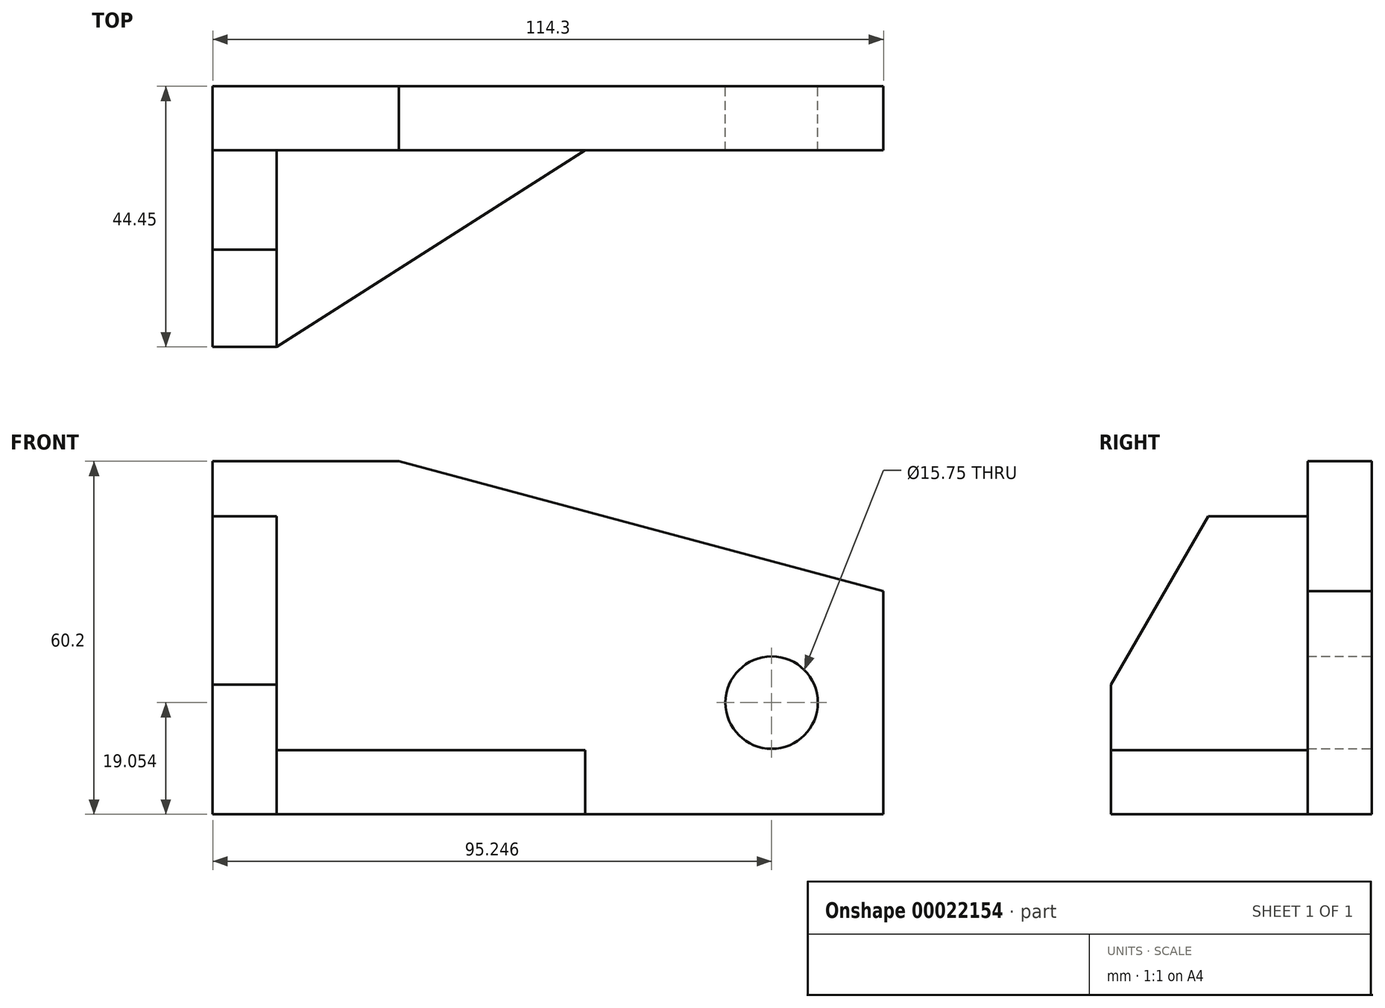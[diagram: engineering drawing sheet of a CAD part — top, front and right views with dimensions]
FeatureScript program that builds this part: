
annotation { "Feature Type Name" : "Feature", "Feature Type Description" : "" }
export const myFeature = defineFeature(function(context is Context, id is Id, definition is map)
    precondition{}
    {
        {
            var Q0;
            Q0=qCreatedBy(makeId("Front.planeOp"),FACE);
            var sketch = newSketch(context, id + "F0", { "sketchPlane" : qUnion([Q0])});
            skLineSegment(sketch, "E0.bottom", {"start": v(-55.11, 32.77) * mm, "end": v(59.19, 32.77) * mm});
            skLineSegment(sketch, "E0.top", {"start": v(-55.11, -27.43) * mm, "end": v(59.19, -27.43) * mm});
            skLineSegment(sketch, "E0.left", {"start": v(-55.11, 32.77) * mm, "end": v(-55.11, -27.43) * mm});
            skLineSegment(sketch, "E0.right", {"start": v(59.19, 32.77) * mm, "end": v(59.19, -27.43) * mm});
            skLineSegment(sketch, "E1", {"start": v(-23.36, 32.77) * mm, "end": v(59.19, 10.65) * mm});
            skCircle(sketch, "E2", {"center": v(40.14, -8.38) * mm, "radius": 7.87 * mm});
            skSolve(sketch);
        }
        {
            var Q0;
            {var subQ2=sQuery(id+"F0.wireOp",EDGE,"E0.top");Q0=makeQuery(id+"F0.imprint","IMPRINT",FACE,{"disambiguationData":[TD([[makeQuery(id+"F0.imprint","IMPRINT",EDGE,{"derivedFrom":subQ2}),1.0]])]});}
            extrude(context, id + "F1", {"entities" : qUnion([Q0]), "depth" : 10.92 * mm});
        }
        {
            var Q0;
            Q0=makeQuery(id+"F1.opExtrude","SWEPT_FACE",FACE,{"disambiguationData":[OSD([sQuery(id+"F0.wireOp",EDGE,"E0.left")])]});
            var sketch = newSketch(context, id + "F2", { "sketchPlane" : qUnion([Q0])});
            skLineSegment(sketch, "E3.bottom", {"start": v(10.92, -27.43) * mm, "end": v(44.45, -27.43) * mm});
            skLineSegment(sketch, "E3.top", {"start": v(10.92, 23.37) * mm, "end": v(44.45, 23.37) * mm});
            skLineSegment(sketch, "E3.left", {"start": v(10.92, -27.43) * mm, "end": v(10.92, 23.37) * mm});
            skLineSegment(sketch, "E3.right", {"start": v(44.45, -27.43) * mm, "end": v(44.45, 23.37) * mm});
            skLineSegment(sketch, "E4", {"start": v(44.45, -5.33) * mm, "end": v(27.88, 23.37) * mm});
            skSolve(sketch);
        }
        {
            var Q0;
            {var subQ2=sQuery(id+"F2.wireOp",EDGE,"E3.bottom");Q0=makeQuery(id+"F2.imprint","IMPRINT",FACE,{"disambiguationData":[TD([[makeQuery(id+"F2.imprint","IMPRINT",EDGE,{"derivedFrom":subQ2}),1.0]])]});}
            extrude(context, id + "F3", {"entities" : qUnion([Q0]), "oppositeDirection" : true, "depth" : 10.92 * mm});
        }
        {
            var Q0;
            Q0=makeQuery(id+"F1.opExtrude","SWEPT_FACE",FACE,{"disambiguationData":[OSD([sQuery(id+"F0.wireOp",EDGE,"E0.top")])]});
            var sketch = newSketch(context, id + "F4", { "sketchPlane" : qUnion([Q0])});
            skLineSegment(sketch, "E5.bottom", {"start": v(-44.2, 44.45) * mm, "end": v(8.39, 44.45) * mm});
            skLineSegment(sketch, "E5.top", {"start": v(-44.2, 10.92) * mm, "end": v(8.39, 10.92) * mm});
            skLineSegment(sketch, "E5.left", {"start": v(-44.2, 44.45) * mm, "end": v(-44.2, 10.92) * mm});
            skLineSegment(sketch, "E5.right", {"start": v(8.39, 44.45) * mm, "end": v(8.39, 10.92) * mm});
            skLineSegment(sketch, "E6", {"start": v(-44.2, 44.45) * mm, "end": v(8.39, 10.92) * mm});
            skSolve(sketch);
        }
        {
            var Q0;
            Q0=makeQuery(id+"F4.imprint","IMPRINT",FACE,{"disambiguationData":[TD([[makeQuery(id+"F4.imprint","IMPRINT",EDGE,{"derivedFrom":sQuery(id+"F4.wireOp",EDGE,"E5.top")}),1.0]])]});
            extrude(context, id + "F5", {"entities" : qUnion([Q0]), "oppositeDirection" : true, "depth" : 10.92 * mm});
        }
    });
